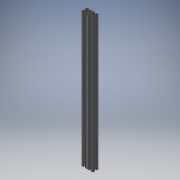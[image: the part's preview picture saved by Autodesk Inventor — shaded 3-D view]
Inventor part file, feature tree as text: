
AUTODESK INVENTOR PART (.ipt)
format: ipt  version: 2018 (Build 220112000, 112)  size: 575,488 bytes
history: native  units: mm
features: other x1, extrude x1, sketch x1
ambient origin geometry x8: Origin, YZ Plane, XZ Plane, XY Plane, X Axis, Y Axis, Z Axis, Center Point
bodies: Body1 (feature_tree)
feature tree (3):
  other  "Sólido1"
  extrude  "Extrusão1"  [1 undecoded]
  sketch  "Esboço1"  dims[d0=700.0mm d1=0.0mm]
note: 1 required parameter value undecoded (feature->parameter linkage not recoverable at this tier; creation-order binding heuristic only, values carry confidence <= 0.55)
